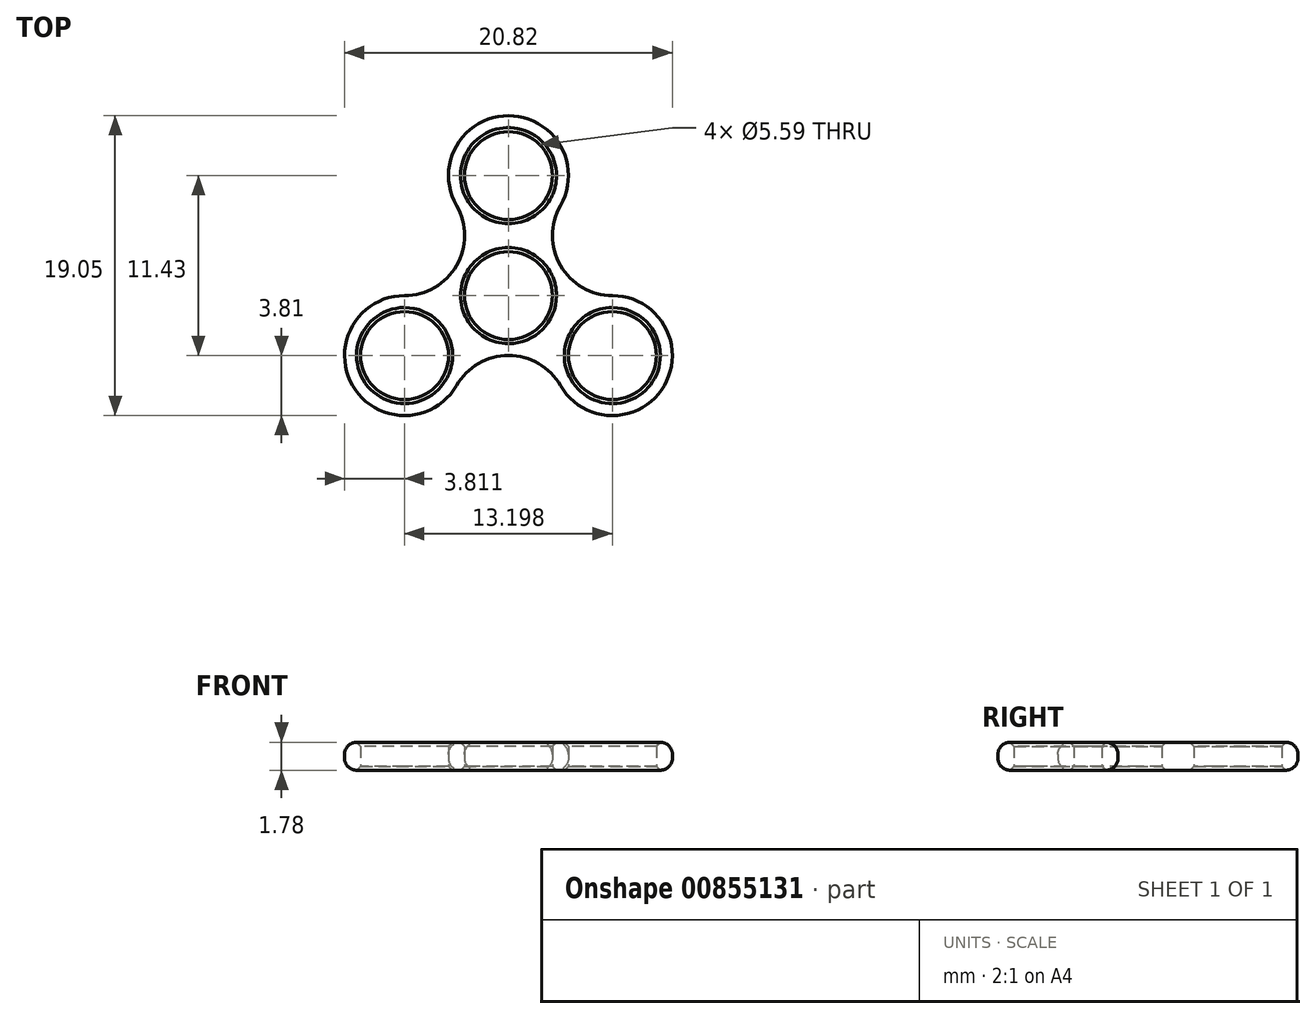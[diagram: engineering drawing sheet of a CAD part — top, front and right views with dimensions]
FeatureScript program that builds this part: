
annotation { "Feature Type Name" : "Feature", "Feature Type Description" : "" }
export const myFeature = defineFeature(function(context is Context, id is Id, definition is map)
    precondition{}
    {
        {
            var Q0;
            Q0=qCreatedBy(makeId("Top.planeOp"),FACE);
            var sketch = newSketch(context, id + "F0", { "sketchPlane" : qUnion([Q0])});
            skCircle(sketch, "E0", {"center": v(0, 0) * mm, "radius": 2.8 * mm});
            skCircle(sketch, "E1", {"center": v(0, 7.62) * mm, "radius": 2.8 * mm});
            skCircle(sketch, "E2.1.0", {"center": v(-6.6, -3.8) * mm, "radius": 2.8 * mm});
            skCircle(sketch, "E2.2.0", {"center": v(6.6, -3.81) * mm, "radius": 2.8 * mm});
            skArc(sketch, "E3.0", {"start": v(3.3, 5.71) * mm, "mid": v(0, 11.43) * mm, "end": v(-3.3, 5.72) * mm});
            skArc(sketch, "E4.0", {"start": v(-6.6, 0) * mm, "mid": v(-9.9, -5.71) * mm, "end": v(-3.3, -5.72) * mm});
            skArc(sketch, "E5.0", {"start": v(3.3, -5.71) * mm, "mid": v(9.9, -5.72) * mm, "end": v(6.6, 0) * mm});
            skLineSegment(sketch, "E6", {"start": v(0, 0) * mm, "end": v(-6.6, -3.8) * mm, "construction": true});
            skLineSegment(sketch, "E7", {"start": v(0, 0) * mm, "end": v(0, 7.62) * mm, "construction": true});
            skLineSegment(sketch, "E8", {"start": v(0, 0) * mm, "end": v(6.6, -3.81) * mm, "construction": true});
            skLineSegment(sketch, "E9", {"start": v(6.6, -3.81) * mm, "end": v(6.6, 0) * mm, "construction": true});
            skLineSegment(sketch, "E10", {"start": v(-6.6, -3.8) * mm, "end": v(-6.6, 0) * mm, "construction": true});
            skLineSegment(sketch, "E11", {"start": v(0, 7.62) * mm, "end": v(-3.3, 5.71) * mm, "construction": true});
            skLineSegment(sketch, "E12.MirrorCS", {"start": v(0, 7.62) * mm, "end": v(3.3, 5.71) * mm, "construction": true});
            skLineSegment(sketch, "E13.MirrorCS", {"start": v(-6.6, -3.8) * mm, "end": v(-3.3, -5.72) * mm, "construction": true});
            skLineSegment(sketch, "E14.MirrorCS", {"start": v(6.6, -3.81) * mm, "end": v(3.3, -5.71) * mm, "construction": true});
            skArc(sketch, "E15", {"start": v(-6.6, 0) * mm, "mid": v(-3.3, 1.9) * mm, "end": v(-3.3, 5.72) * mm});
            skArc(sketch, "E16", {"start": v(3.3, 5.71) * mm, "mid": v(3.3, 1.9) * mm, "end": v(6.6, 0) * mm});
            skArc(sketch, "E17", {"start": v(3.3, -5.71) * mm, "mid": v(0, -3.81) * mm, "end": v(-3.3, -5.72) * mm});
            skSolve(sketch);
        }
        {
            var Q0;
            Q0=makeQuery(id+"F0.imprint","IMPRINT",FACE,{"disambiguationData":[TD([[makeQuery(id+"F0.imprint","IMPRINT",EDGE,{"derivedFrom":sQuery(id+"F0.wireOp",EDGE,"E0")}),-1.0]])]});
            extrude(context, id + "F1", {"entities" : qUnion([Q0]), "depth" : 1.78 * mm, "offsetDistance" : 25.4 * mm});
        }
        {
            var Q0;
            Q0=makeQuery(id+"F1.opExtrude","CAP_EDGE",EDGE,{"disambiguationData":[OSD([sQuery(id+"F0.wireOp",EDGE,"E17")])],"isStart":true});
            var Q1;
            Q1=makeQuery(id+"F1.opExtrude","CAP_EDGE",EDGE,{"disambiguationData":[OSD([sQuery(id+"F0.wireOp",EDGE,"E17")])],"isStart":false});
            fillet(context, id + "F2", {"entities" : qUnion([Q0, Q1]), "radius" : 0.76 * mm, "tangentPropagation" : true, "allowEdgeOverflow" : false});
        }
        {
            var Q0;
            Q0=makeQuery(id+"F1.opExtrude","CAP_EDGE",EDGE,{"disambiguationData":[OSD([sQuery(id+"F0.wireOp",EDGE,"E0")])],"isStart":true});
            var Q1;
            Q1=makeQuery(id+"F1.opExtrude","CAP_EDGE",EDGE,{"disambiguationData":[OSD([sQuery(id+"F0.wireOp",EDGE,"E2.2.0")])],"isStart":true});
            var Q2;
            Q2=makeQuery(id+"F1.opExtrude","CAP_EDGE",EDGE,{"disambiguationData":[OSD([sQuery(id+"F0.wireOp",EDGE,"E2.2.0")])],"isStart":false});
            var Q3;
            Q3=makeQuery(id+"F1.opExtrude","CAP_EDGE",EDGE,{"disambiguationData":[OSD([sQuery(id+"F0.wireOp",EDGE,"E0")])],"isStart":false});
            var Q4;
            Q4=makeQuery(id+"F1.opExtrude","CAP_EDGE",EDGE,{"disambiguationData":[OSD([sQuery(id+"F0.wireOp",EDGE,"E1")])],"isStart":true});
            var Q5;
            Q5=makeQuery(id+"F1.opExtrude","CAP_EDGE",EDGE,{"disambiguationData":[OSD([sQuery(id+"F0.wireOp",EDGE,"E1")])],"isStart":false});
            var Q6;
            Q6=makeQuery(id+"F1.opExtrude","CAP_EDGE",EDGE,{"disambiguationData":[OSD([sQuery(id+"F0.wireOp",EDGE,"E2.1.0")])],"isStart":true});
            var Q7;
            Q7=makeQuery(id+"F1.opExtrude","CAP_EDGE",EDGE,{"disambiguationData":[OSD([sQuery(id+"F0.wireOp",EDGE,"E2.1.0")])],"isStart":false});
            chamfer(context, id + "F3", {"entities" : qUnion([Q0, Q1, Q2, Q3, Q4, Q5, Q6, Q7]), "width" : 0.25 * mm});
        }
    });
